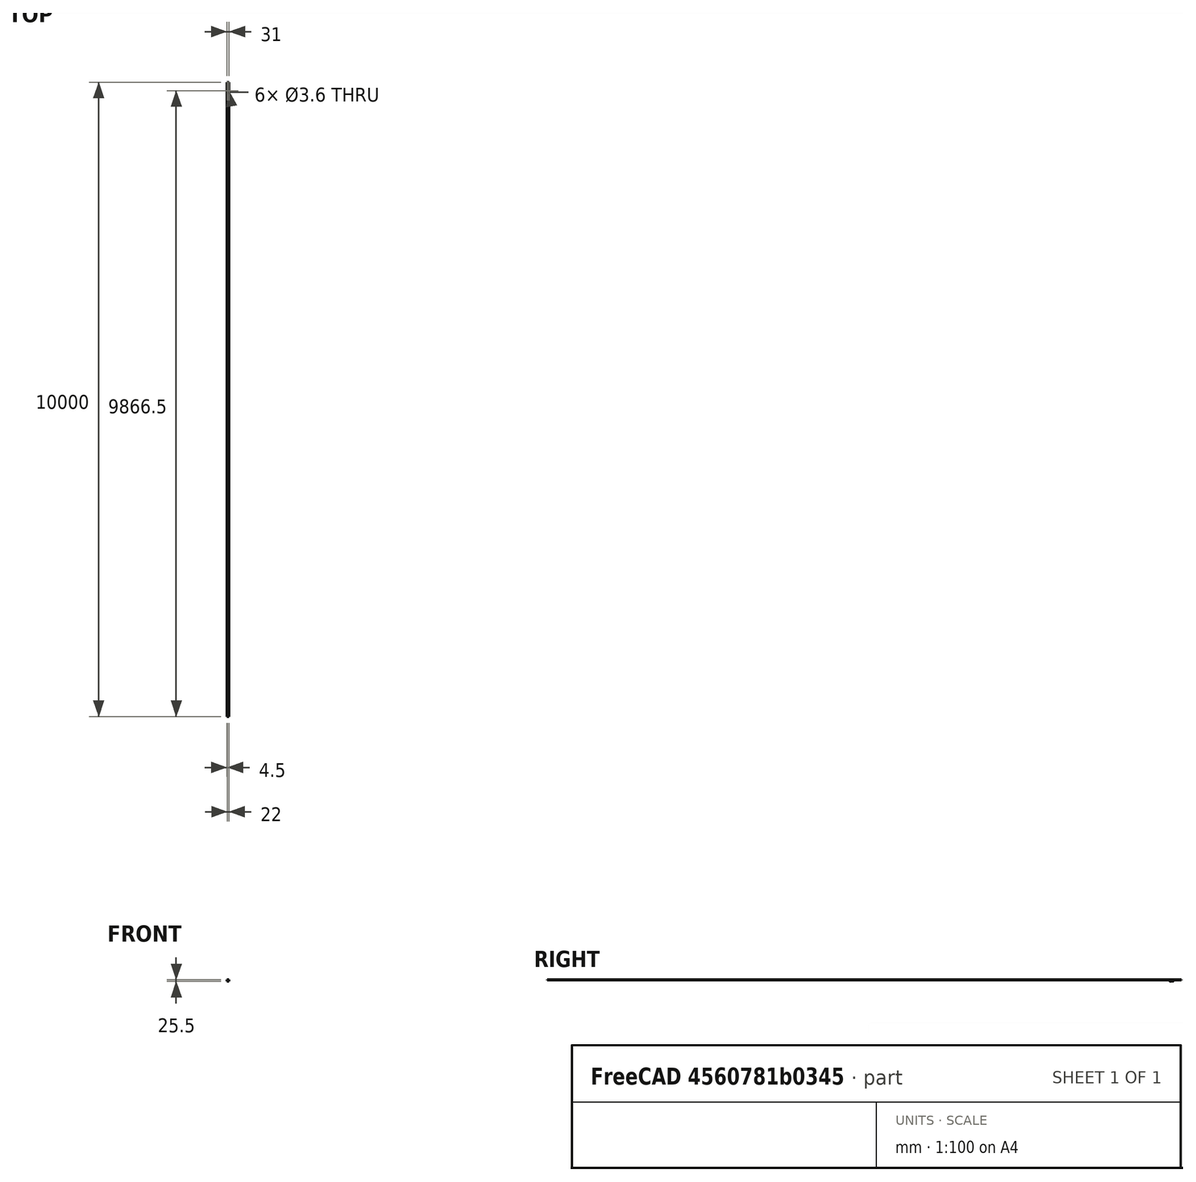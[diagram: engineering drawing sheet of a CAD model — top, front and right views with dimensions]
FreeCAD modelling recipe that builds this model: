
FCSTD DOCUMENT  (FreeCAD 0.15R4671 (Git))
Label: TopCornerRodBracket
License: All rights reserved
LicenseURL: http://en.wikipedia.org/wiki/All_rights_reserved
objects: Sketcher::SketchObject×4, Mesh::Feature×3, PartDesign::Pocket×3, PartDesign::Fillet×3, Part::Feature×2, PartDesign::Pad×1
note: 17 computed .brp shape members not serialized (recipe doc carries the construction recipe); baked Part::Feature solids carry a one-line shape summary decoded from their .brp

FEATURE [Sketcher::SketchObject] Sketch
  Placement = pos=(0,0,0) rot=(1,0,0;3.14159rad)
  sketch-geometry (6):
    g0: LineSegment StartX=51 StartY=69.5 StartZ=0 EndX=21 EndY=69.5 EndZ=0
    g1: LineSegment StartX=21 StartY=69.5 StartZ=0 EndX=21 EndY=58.5 EndZ=0
    g2: LineSegment StartX=21 StartY=58.5 StartZ=0 EndX=51 EndY=58.5 EndZ=0
    g3: LineSegment StartX=51 StartY=58.5 StartZ=0 EndX=51 EndY=69.5 EndZ=0
    g4: Circle CenterX=47 CenterY=64 CenterZ=0 NormalX=0 NormalY=0 NormalZ=1 Radius=1.8
    g5: Circle CenterX=25 CenterY=64 CenterZ=0 NormalX=0 NormalY=0 NormalZ=1 Radius=1.8
  constraints (18):
    c: Coincident(g0,g1)
    c: Coincident(g1,g2)
    c: Coincident(g2,g3)
    c: Coincident(g3,g0)
    c: Horizontal(g0)
    c: Horizontal(g2)
    c: Vertical(g1)
    c: Vertical(g3)
    c: DistanceY(g0,g1) = -11
    c: DistanceX(g0,g0) = 30
    c: DistanceX(g1) = 21
    c: DistanceY(g1) = 58.5
    c: Radius(g4) = 1.8
    c: Radius(g5) = 1.8
    c: DistanceX(g5,g4) = 22
    c: DistanceY(g5,g4) = 0
    c: DistanceX(g5,g1) = -4
    c: DistanceY(g5,g1) = -5.5
FEATURE [Part::Feature] LM8UU_8mm_Linear_Bearing
  Placement = pos=(36,-114.5,-5.5) rot=(0,0,1;1.5708rad)
  shape: bbox 15 x 24 x 15 mm, 34 faces (baked)
FEATURE [Mesh::Feature] _mmRod_x100mm  label="8mmRod_x100mm"
  Placement = pos=(36,-160.5,-5.5) rot=(0,0,1;3.14159rad)
FEATURE [PartDesign::Pad] Pad
  Length = 11.5
  Length2 = 100
  Placement = pos=(0,0,0) rot=(1,0,0;3.14159rad)
  Sketch = -> Sketch
  Type = 0
FEATURE [Sketcher::SketchObject] Sketch001
  Placement = pos=(0,-69.5,0) rot=(0,0.707107,-0.707107;3.14159rad)
  Support = -> Pad [Face1]
  sketch-geometry (6):
    g0: ArcOfCircle CenterX=-36 CenterY=5.5 CenterZ=0 NormalX=0 NormalY=0 NormalZ=1 Radius=6 StartAngle=0 EndAngle=3.14159
    g1: LineSegment StartX=-30 StartY=5.5 StartZ=0 EndX=-20.5 EndY=5.5 EndZ=0
    g2: LineSegment StartX=-20.5 StartY=5.5 StartZ=0 EndX=-20.5 EndY=12.5 EndZ=0
    g3: LineSegment StartX=-20.5 StartY=12.5 StartZ=0 EndX=-51.5 EndY=12.5 EndZ=0
    g4: LineSegment StartX=-51.5 StartY=12.5 StartZ=0 EndX=-51.5 EndY=5.5 EndZ=0
    g5: LineSegment StartX=-51.5 StartY=5.5 StartZ=0 EndX=-42 EndY=5.5 EndZ=0
  constraints (6):
    c: Coincident(g1,g2)
    c: Coincident(g2,g3)
    c: Coincident(g3,g4)
    c: Coincident(g4,g5)
    c: Coincident(g0,g5)
    c: Coincident(g0,g1)
FEATURE [PartDesign::Pocket] Pocket
  Length = 5
  Placement = pos=(0,0,0) rot=(1,0,0;3.14159rad)
  Sketch = -> Sketch001
  Type = 1
FEATURE [Mesh::Feature] HexNutStyle1_M  label="HexNutStyle1_M3"
  Placement = pos=(39.2,-42,-122) rot=(0,0,1;0rad)
FEATURE [Mesh::Feature] HexNutStyle1_M001  label="HexNutStyle1_M004"
  Placement = pos=(61.2,-42,-122) rot=(0,0,1;0rad)
FEATURE [Sketcher::SketchObject] Sketch002
  Placement = pos=(0,0,-5.5) rot=(1,0,0;3.14159rad)
  Support = -> Pocket [Face4]
  sketch-geometry (14):
    g0: LineSegment StartX=25 StartY=67.5 StartZ=0 EndX=21.9689 EndY=65.75 EndZ=0
    g1: LineSegment StartX=21.9689 StartY=65.75 StartZ=0 EndX=21.9689 EndY=62.25 EndZ=0
    g2: LineSegment StartX=21.9689 StartY=62.25 StartZ=0 EndX=25 EndY=60.5 EndZ=0
    g3: LineSegment StartX=25 StartY=60.5 StartZ=0 EndX=28.0311 EndY=62.25 EndZ=0
    g4: LineSegment StartX=28.0311 StartY=62.25 StartZ=0 EndX=28.0311 EndY=65.75 EndZ=0
    g5: LineSegment StartX=28.0311 StartY=65.75 StartZ=0 EndX=25 EndY=67.5 EndZ=0
    g6: Circle [constr] CenterX=25 CenterY=64 CenterZ=0 NormalX=0 NormalY=0 NormalZ=1 Radius=3.5
    g7: LineSegment StartX=47 StartY=67.5 StartZ=0 EndX=43.9689 EndY=65.75 EndZ=0
    g8: LineSegment StartX=43.9689 StartY=65.75 StartZ=0 EndX=43.9689 EndY=62.25 EndZ=0
    g9: LineSegment StartX=43.9689 StartY=62.25 StartZ=0 EndX=47 EndY=60.5 EndZ=0
    g10: LineSegment StartX=47 StartY=60.5 StartZ=0 EndX=50.0311 EndY=62.25 EndZ=0
    g11: LineSegment StartX=50.0311 StartY=62.25 StartZ=0 EndX=50.0311 EndY=65.75 EndZ=0
    g12: LineSegment StartX=50.0311 StartY=65.75 StartZ=0 EndX=47 EndY=67.5 EndZ=0
    g13: Circle [constr] CenterX=47 CenterY=64 CenterZ=0 NormalX=0 NormalY=0 NormalZ=1 Radius=3.5
  constraints (26):
    c: Coincident(g0,g1)
    c: Coincident(g1,g2)
    c: Coincident(g2,g3)
    c: Coincident(g3,g4)
    c: Coincident(g4,g5)
    c: Coincident(g5,g0)
    c: Equal(g0, g1-g5) x5
    c: PointOnObject(g0,g6)
    c: PointOnObject(g1,g6)
    c: PointOnObject(g2,g6)
    c: PointOnObject(g3,g6)
    c: PointOnObject(g4,g6)
    c: PointOnObject(g5,g6)
    c: Coincident(g7,g8)
    c: Coincident(g8,g9)
    c: Coincident(g9,g10)
    c: Coincident(g10,g11)
    c: Coincident(g11,g12)
    c: Coincident(g12,g7)
    c: Equal(g7, g8-g12) x5
    c: PointOnObject(g7,g13)
    c: PointOnObject(g8,g13)
    c: PointOnObject(g9,g13)
    c: PointOnObject(g10,g13)
    c: PointOnObject(g11,g13)
    c: PointOnObject(g12,g13)
FEATURE [PartDesign::Pocket] Pocket001
  Length = 3
  Placement = pos=(0,0,0) rot=(1,0,0;3.14159rad)
  Sketch = -> Sketch002
  Type = 0
FEATURE [PartDesign::Fillet] Fillet
  Base = -> Pocket001 [Edge13,Edge2,Edge35,Edge7]
  Placement = pos=(0,0,0) rot=(1,0,0;3.14159rad)
  Radius = 2
FEATURE [PartDesign::Fillet] Fillet001
  Base = -> Fillet [Edge21,Edge31]
  Placement = pos=(0,0,0) rot=(1,0,0;3.14159rad)
  Radius = 2
FEATURE [PartDesign::Fillet] Fillet002
  Base = -> Fillet001 [Edge4]
  Placement = pos=(0,0,0) rot=(1,0,0;3.14159rad)
  Radius = 1
FEATURE [Part::Feature] Fillet003  label="TopRodHolder_noRodHole"
  shape: bbox 30.16 x 11.33 x 11.99 mm, 56 faces (baked)
FEATURE [Sketcher::SketchObject] Sketch003
  Placement = pos=(0,-69.5,0) rot=(1,0,0;1.5708rad)
  Support = -> Fillet003 [Face1]
  sketch-geometry (1):
    g0: Circle CenterX=36 CenterY=-5.5 CenterZ=0 NormalX=0 NormalY=0 NormalZ=1 Radius=4.2
  constraints (1):
    c: Radius(g0) = 4.2
FEATURE [PartDesign::Pocket] Pocket002  label="TopRodHolder"
  Length = 10
  Sketch = -> Sketch003
  Type = 0
